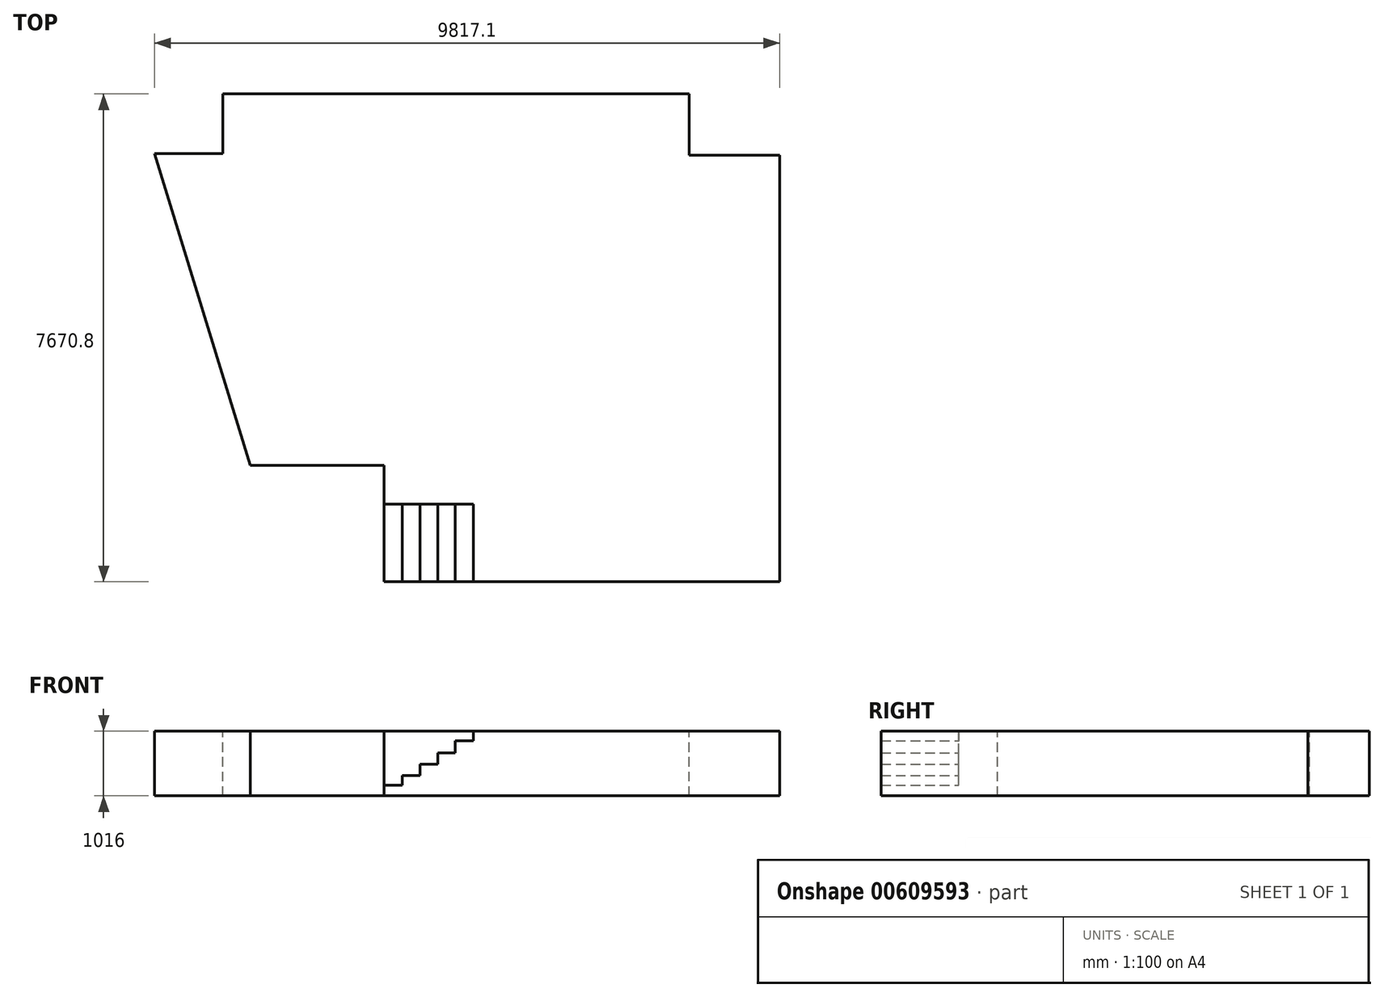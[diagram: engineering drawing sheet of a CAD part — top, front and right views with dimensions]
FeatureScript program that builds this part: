
annotation { "Feature Type Name" : "Feature", "Feature Type Description" : "" }
export const myFeature = defineFeature(function(context is Context, id is Id, definition is map)
    precondition{}
    {
        {
            var Q0;
            Q0=qCreatedBy(makeId("Top.planeOp"),FACE);
            var sketch = newSketch(context, id + "F0", { "sketchPlane" : qUnion([Q0])});
            skLineSegment(sketch, "E0", {"start": v(-608.02, -147.72) * mm, "end": v(6719.88, -147.72) * mm});
            skLineSegment(sketch, "E1", {"start": v(6719.88, -147.72) * mm, "end": v(6719.88, -1112.92) * mm});
            skLineSegment(sketch, "E2", {"start": v(6719.88, -1112.92) * mm, "end": v(8142.28, -1112.92) * mm});
            skLineSegment(sketch, "E3", {"start": v(8142.28, -1112.92) * mm, "end": v(8142.28, -6599.32) * mm});
            skLineSegment(sketch, "E4", {"start": v(8142.28, -6599.32) * mm, "end": v(1931.98, -6599.32) * mm});
            skLineSegment(sketch, "E5", {"start": v(1931.98, -6599.32) * mm, "end": v(1931.98, -5989.72) * mm});
            skLineSegment(sketch, "E6", {"start": v(1931.98, -5989.72) * mm, "end": v(-176.22, -5989.72) * mm});
            skLineSegment(sketch, "E7", {"start": v(-608.02, -147.72) * mm, "end": v(-608.02, -1087.52) * mm});
            skLineSegment(sketch, "E8", {"start": v(-608.02, -1087.52) * mm, "end": v(-1674.82, -1087.52) * mm});
            skLineSegment(sketch, "E9", {"start": v(-1674.82, -1087.52) * mm, "end": v(-176.22, -5989.72) * mm});
            skSolve(sketch);
        }
        {
            var Q0;
            Q0 = qSketchRegion(id + "F0", true);
            extrude(context, id + "F1", {"entities" : qUnion([Q0]), "oppositeDirection" : true, "depth" : 1016 * mm, "offsetDistance" : 25.4 * mm});
        }
        {
            var Q0;
            Q0=makeQuery(id+"F1.opExtrude","SWEPT_FACE",FACE,{"disambiguationData":[OSD([sQuery(id+"F0.wireOp",EDGE,"E4")])]});
            var sketch = newSketch(context, id + "F2", { "sketchPlane" : qUnion([Q0])});
            skLineSegment(sketch, "E10.bottom", {"start": v(8142.28, 0) * mm, "end": v(3328.98, 0) * mm});
            skLineSegment(sketch, "E10.top", {"start": v(8142.28, -1016) * mm, "end": v(3328.98, -1016) * mm});
            skLineSegment(sketch, "E10.left", {"start": v(8142.28, 0) * mm, "end": v(8142.28, -1016) * mm});
            skLineSegment(sketch, "E10.right", {"start": v(3328.98, 0) * mm, "end": v(3328.98, -1016) * mm});
            skLineSegment(sketch, "E11.bottom", {"start": v(3328.98, -1016) * mm, "end": v(3049.58, -1016) * mm});
            skLineSegment(sketch, "E11.top", {"start": v(3328.98, -152.4) * mm, "end": v(3049.58, -152.4) * mm});
            skLineSegment(sketch, "E11.left", {"start": v(3328.98, -1016) * mm, "end": v(3328.98, -152.4) * mm});
            skLineSegment(sketch, "E11.right", {"start": v(3049.58, -1016) * mm, "end": v(3049.58, -152.4) * mm});
            skLineSegment(sketch, "E12.bottom", {"start": v(3049.58, -1016) * mm, "end": v(2770.18, -1016) * mm});
            skLineSegment(sketch, "E12.top", {"start": v(3049.58, -342.9) * mm, "end": v(2770.18, -342.9) * mm});
            skLineSegment(sketch, "E12.left", {"start": v(3049.58, -1016) * mm, "end": v(3049.58, -342.9) * mm});
            skLineSegment(sketch, "E12.right", {"start": v(2770.18, -1016) * mm, "end": v(2770.18, -342.9) * mm});
            skLineSegment(sketch, "E13.bottom", {"start": v(2770.18, -1016) * mm, "end": v(2490.78, -1016) * mm});
            skLineSegment(sketch, "E13.top", {"start": v(2770.18, -520.7) * mm, "end": v(2490.78, -520.7) * mm});
            skLineSegment(sketch, "E13.left", {"start": v(2770.18, -1016) * mm, "end": v(2770.18, -520.7) * mm});
            skLineSegment(sketch, "E13.right", {"start": v(2490.78, -1016) * mm, "end": v(2490.78, -520.7) * mm});
            skLineSegment(sketch, "E14.bottom", {"start": v(2490.78, -1016) * mm, "end": v(2211.38, -1016) * mm});
            skLineSegment(sketch, "E14.top", {"start": v(2490.78, -698.5) * mm, "end": v(2211.38, -698.5) * mm});
            skLineSegment(sketch, "E14.left", {"start": v(2490.78, -1016) * mm, "end": v(2490.78, -698.5) * mm});
            skLineSegment(sketch, "E14.right", {"start": v(2211.38, -1016) * mm, "end": v(2211.38, -698.5) * mm});
            skLineSegment(sketch, "E15.bottom", {"start": v(2211.38, -1016) * mm, "end": v(1931.98, -1016) * mm});
            skLineSegment(sketch, "E15.top", {"start": v(2211.38, -850.9) * mm, "end": v(1931.98, -850.9) * mm});
            skLineSegment(sketch, "E15.left", {"start": v(2211.38, -1016) * mm, "end": v(2211.38, -850.9) * mm});
            skLineSegment(sketch, "E15.right", {"start": v(1931.98, -1016) * mm, "end": v(1931.98, -850.9) * mm});
            skSolve(sketch);
        }
        {
            var Q0;
            Q0 = qSketchRegion(id + "F2", true);
            extrude(context, id + "F3", {"entities" : qUnion([Q0]), "operationType" : NewBodyOperationType.ADD, "depth" : 1219.2 * mm, "offsetDistance" : 25.4 * mm});
        }
    });
